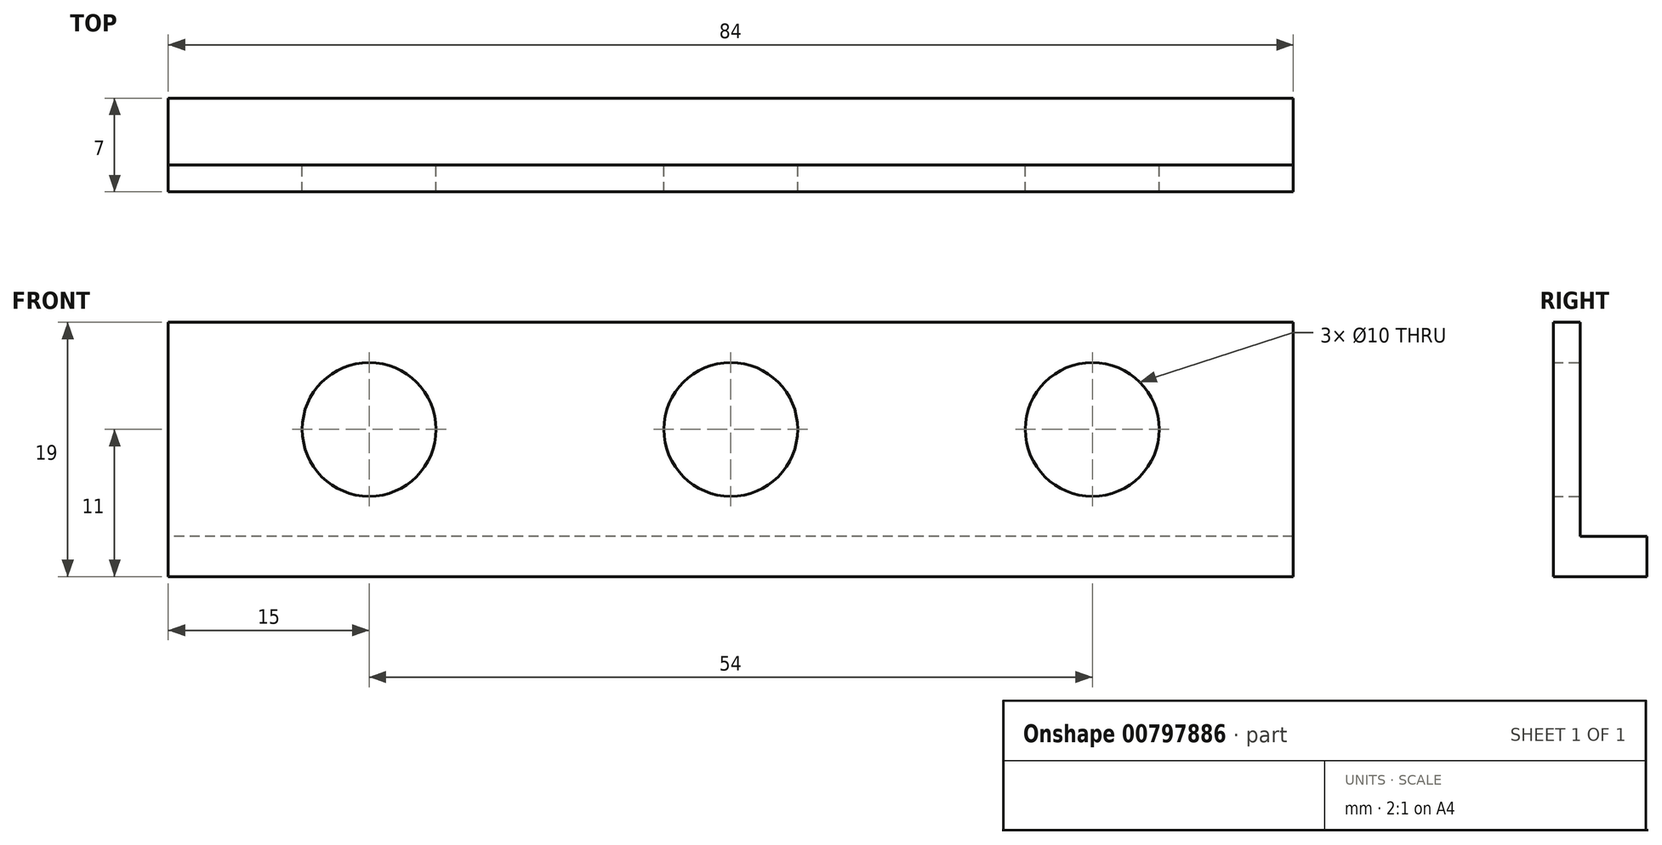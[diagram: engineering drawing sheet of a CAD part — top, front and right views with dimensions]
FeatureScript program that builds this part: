
annotation { "Feature Type Name" : "Feature", "Feature Type Description" : "" }
export const myFeature = defineFeature(function(context is Context, id is Id, definition is map)
    precondition{}
    {
        {
            var Q0;
            Q0=qCreatedBy(makeId("Front.planeOp"),FACE);
            var sketch = newSketch(context, id + "F0", { "sketchPlane" : qUnion([Q0])});
            skLineSegment(sketch, "E0.bottom", {"start": v(42, 8) * mm, "end": v(-42, 8) * mm});
            skLineSegment(sketch, "E0.top", {"start": v(42, -8) * mm, "end": v(-42, -8) * mm});
            skLineSegment(sketch, "E0.left", {"start": v(42, 8) * mm, "end": v(42, -8) * mm});
            skLineSegment(sketch, "E0.right", {"start": v(-42, 8) * mm, "end": v(-42, -8) * mm});
            skPoint(sketch, "E0.middle", {"position": v(0, 0) * mm});
            skCircle(sketch, "E1", {"center": v(0, 0) * mm, "radius": 5 * mm});
            skCircle(sketch, "E2", {"center": v(-27, 0) * mm, "radius": 5 * mm});
            skCircle(sketch, "E3", {"center": v(27, 0) * mm, "radius": 5 * mm});
            skLineSegment(sketch, "E4.bottom", {"start": v(-42, -8) * mm, "end": v(42, -8) * mm});
            skLineSegment(sketch, "E4.top", {"start": v(-42, -11) * mm, "end": v(42, -11) * mm});
            skLineSegment(sketch, "E4.left", {"start": v(-42, -8) * mm, "end": v(-42, -11) * mm});
            skLineSegment(sketch, "E4.right", {"start": v(42, -8) * mm, "end": v(42, -11) * mm});
            skSolve(sketch);
        }
        {
            var Q0;
            Q0=qSketchRegion(id+"F0",true);
            extrude(context, id + "F1", {"entities" : qUnion([Q0]), "depth" : 2 * mm, "offsetDistance" : 25 * mm});
        }
        {
            var Q0;
            Q0=makeQuery(id+"F1.opExtrude","CAP_FACE",FACE,{"disambiguationData":[OSD([sQuery(id+"F0.wireOp",EDGE,"E0.bottom"),sQuery(id+"F0.wireOp",EDGE,"E0.left"),sQuery(id+"F0.wireOp",EDGE,"E0.right"),sQuery(id+"F0.wireOp",EDGE,"E1"),sQuery(id+"F0.wireOp",EDGE,"E2"),sQuery(id+"F0.wireOp",EDGE,"E3"),sQuery(id+"F0.wireOp",EDGE,"E4.top"),sQuery(id+"F0.wireOp",EDGE,"E4.left"),sQuery(id+"F0.wireOp",EDGE,"E4.right")])],"isStart":true});
            var sketch = newSketch(context, id + "F2", { "sketchPlane" : qUnion([Q0])});
            skLineSegment(sketch, "E5.bottom", {"start": v(-42, -11) * mm, "end": v(42, -11) * mm});
            skLineSegment(sketch, "E5.top", {"start": v(-42, -8) * mm, "end": v(42, -8) * mm});
            skLineSegment(sketch, "E5.left", {"start": v(-42, -11) * mm, "end": v(-42, -8) * mm});
            skLineSegment(sketch, "E5.right", {"start": v(42, -11) * mm, "end": v(42, -8) * mm});
            skSolve(sketch);
        }
        {
            var Q0;
            Q0=qSketchRegion(id+"F2",true);
            extrude(context, id + "F3", {"entities" : qUnion([Q0]), "operationType" : NewBodyOperationType.ADD, "depth" : 5 * mm, "offsetDistance" : 25 * mm});
        }
    });
